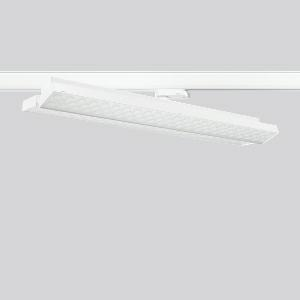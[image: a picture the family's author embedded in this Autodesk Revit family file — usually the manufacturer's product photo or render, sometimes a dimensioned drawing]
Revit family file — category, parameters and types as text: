
# Revit family: tx-move_742162_002_2fa9
name_source: partatom
category: Lighting Fixtures
units: mm (PartAtom-declared; Revit-internal decimal feet)

## family parameters
Cut with Voids When Loaded = No
Host = Face
Light Source = No
Part Type = Normal
Room Calculation Point = No
Round Connector Dimension = Use Diameter
Shared = No

## types (1)
- MultiLumen 1 (1 x LED Modul 830, 2925 lm, 3000)
    Apparent Load = 41 VA
    CIE Flux Codes = 77 96 99 100 100
    Color Rendering = 80
    Color Temperature = 3000
    Default Elevation = 1800 mm
    Description = Series: TX-MOVE
Multifunctional surface-mounted spotlight for area lighting. Very flat design. Housing: sheet steel, powder-coated. Rotation range: 356°. Swivel range: 90°. Consistent alignment possible with visible tilt scale. High-efficiency LED units with optimum light control thanks to clear plastic (PC) lens optics. Spezielle Mikrostrukturen reduzieren Gelbsaum. Symmetrical light distribution. With multi adaptor for 3-circuit tracks 230 V. Suitable for Track on ceiling. MultiLumen: Luminous flux adjustable in 3 steps. Factory setting is the highest luminous flux. Environmentally friendly and resource-saving due to replaceable and recyclable components. 
Colour: traffic white, matt (RAL 9016)
Length: 570 mm
Width: 119 mm
Height: 92 mm
Lamp: LED
Socket: without socket
Colour temperature: 3000K
Colour rendering index (CRI): 80
System power: 41 W
Rated luminous flux: 5850 lm
Luminous efficiency: 143 lm/W
System power 2: 57 W
Rated luminous flux 2: 7950 lm
Luminous efficiency 2: 139 lm/W
System power 3: 73 W
Rated luminous flux 3: 9700 lm
Luminous efficiency 3: 133 lm/W
Control gear: Regulated power supply
Protection class: I
Type of protection: IP 20
    Height = 75 mm
    Lamp = 1 x LED Modul 830
    Lamp Light Flux = 2925 lm
    Lamp count = 1
    Length = 569 mm
    Lifetime = 50000 h
    Luminous efficacy = 143 lm/W
    Manufacturer = RZB
    ModVariant = No
    Model = 742162.002
    Mounting Place = Ceiling
    Mounting Type = Surface mounted
    Number of Poles = 1
    OnlyDefault = Yes
    Power Factor = 1
    Product Name = TX-MOVE
    Product group = Track mounted projectors
    ProductGroupID = 301
    Protection Class = Protection class I
    Protection Degree = IP 20
    RLX_Detail_Level = 1
    RLX_Emergency_Light_Flux = 0 lm
    RLX_Emergency_Type = 0
    RLX_Emergency_Type_DB = No
    RlxData = <blob elided: 31089 chars, md5=51120066>
    Socket = socket
    Standby Power = 0 W
    System Light Flux = 5850 lm
    System Power = 41 W
    Type Comments = MultiLumen 1
    Type Image = 742162.002.jpg
    URL = http://relux.com
    VarID = multilumen_1
    Voltage = 0 V
    Weight = 0.00 kg
    Width = 119 mm

## geometry (parser evidence)
native form markers: Blend x4, Sweep x15
no freeform markers — native parametric forms only
